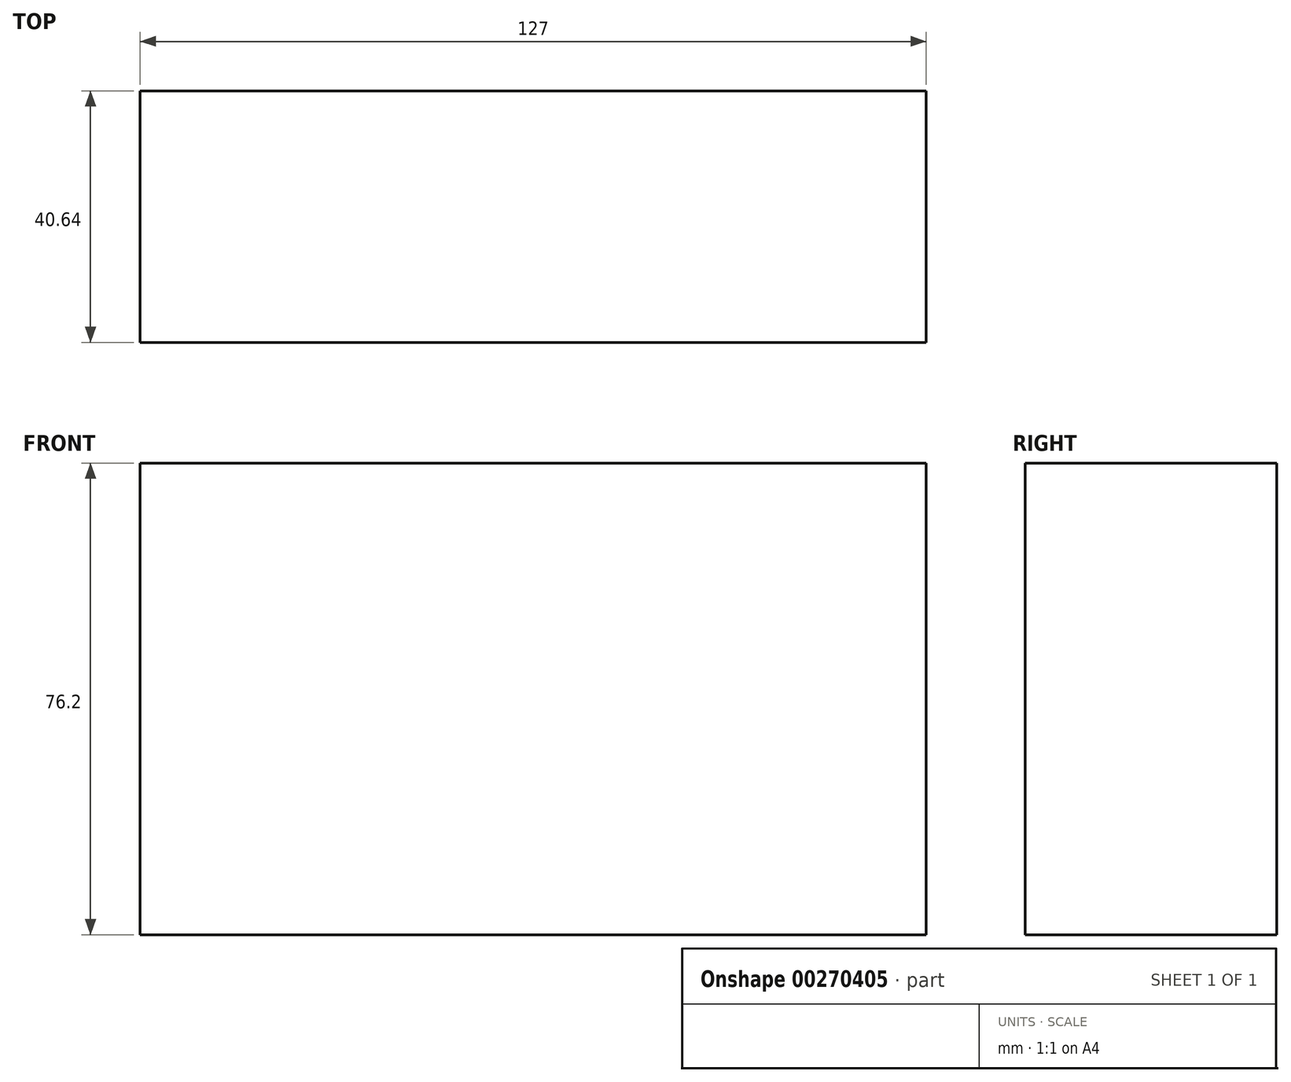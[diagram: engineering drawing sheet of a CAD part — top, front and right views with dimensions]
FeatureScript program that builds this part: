
annotation { "Feature Type Name" : "Feature", "Feature Type Description" : "" }
export const myFeature = defineFeature(function(context is Context, id is Id, definition is map)
    precondition{}
    {
        {
            var Q0;
            Q0=qCreatedBy(makeId("Front.planeOp"),FACE);
            var sketch = newSketch(context, id + "F0", { "sketchPlane" : qUnion([Q0])});
            skLineSegment(sketch, "E0.bottom", {"start": v(-63.5, 38.1) * mm, "end": v(63.5, 38.1) * mm});
            skLineSegment(sketch, "E0.top", {"start": v(-63.5, -38.1) * mm, "end": v(63.5, -38.1) * mm});
            skLineSegment(sketch, "E0.left", {"start": v(-63.5, 38.1) * mm, "end": v(-63.5, -38.1) * mm});
            skLineSegment(sketch, "E0.right", {"start": v(63.5, 38.1) * mm, "end": v(63.5, -38.1) * mm});
            skPoint(sketch, "E0.middle", {"position": v(0, 0) * mm});
            skLineSegment(sketch, "E1", {"start": v(0, 38.1) * mm, "end": v(0, -38.1) * mm});
            skPoint(sketch, "E2", {"position": v(25.4, 0) * mm});
            skPoint(sketch, "E3.MirrorP", {"position": v(-25.4, 0) * mm});
            skSolve(sketch);
        }
        {
            var Q0;
            {var subQ0=sQuery(id+"F0.wireOp",EDGE,"E0.right");Q0=makeQuery(id+"F0.imprint","IMPRINT",FACE,{"disambiguationData":[TD([[makeQuery(id+"F0.imprint","IMPRINT",EDGE,{"derivedFrom":subQ0}),-1.0]])]});}
            var Q1;
            {var subQ0=sQuery(id+"F0.wireOp",EDGE,"E0.left");Q1=makeQuery(id+"F0.imprint","IMPRINT",FACE,{"disambiguationData":[TD([[makeQuery(id+"F0.imprint","IMPRINT",EDGE,{"derivedFrom":subQ0}),1.0]])]});}
            extrude(context, id + "F1", {"entities" : qUnion([Q0, Q1]), "oppositeDirection" : true, "offsetDistance" : 25.4 * mm, "depth" : 40.64 * mm});
        }
    });
